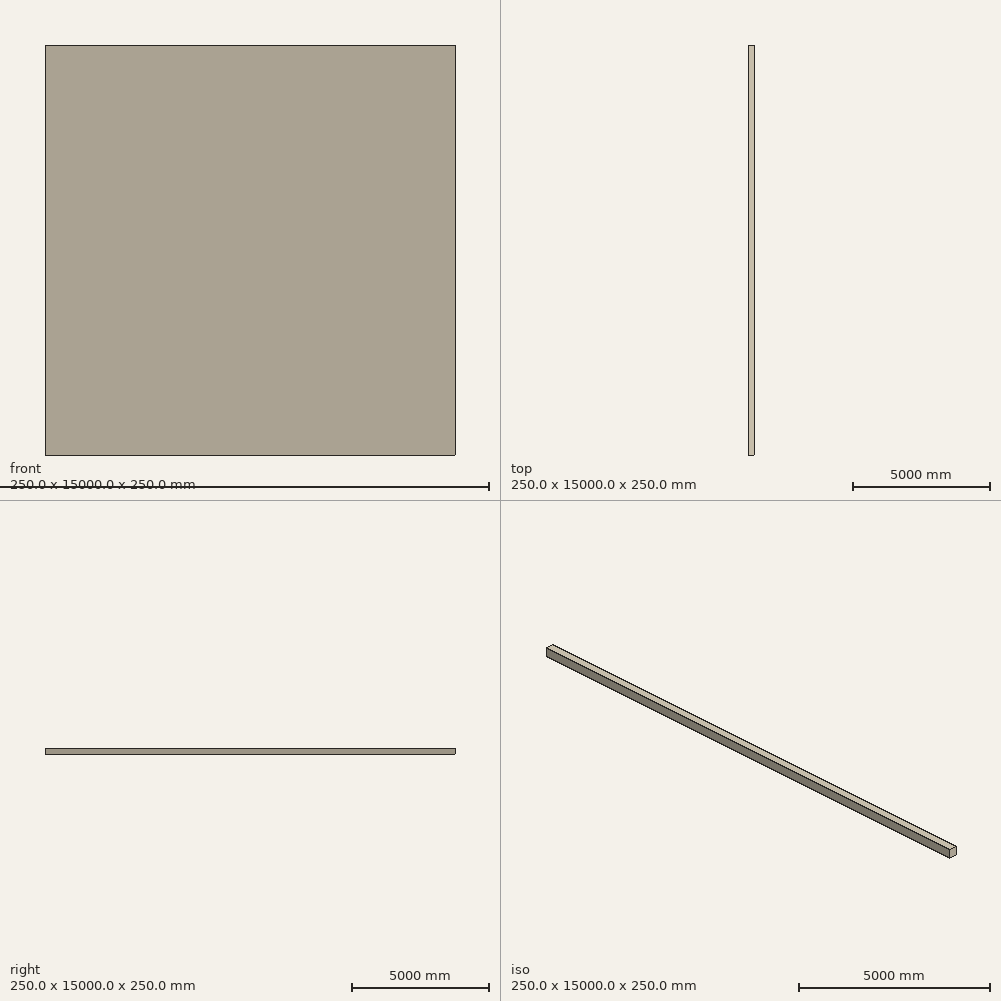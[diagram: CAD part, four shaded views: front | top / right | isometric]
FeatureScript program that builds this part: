
annotation { "Feature Type Name" : "Feature", "Feature Type Description" : "" }
export const myFeature = defineFeature(function(context is Context, id is Id, definition is map)
    precondition{}
    {
        {
            var Q0;
            Q0=qCreatedBy(makeId("Front.planeOp"),FACE);
            var sketch = newSketch(context, id + "F0", { "sketchPlane" : qUnion([Q0])});
            skLineSegment(sketch, "E0.bottom", {"start": v(-124.54, 145.9) * mm, "end": v(125.46, 145.9) * mm});
            skLineSegment(sketch, "E0.top", {"start": v(-124.54, -104.1) * mm, "end": v(125.46, -104.1) * mm});
            skLineSegment(sketch, "E0.left", {"start": v(-124.54, 145.9) * mm, "end": v(-124.54, -104.1) * mm});
            skLineSegment(sketch, "E0.right", {"start": v(125.46, 145.9) * mm, "end": v(125.46, -104.1) * mm});
            skSolve(sketch);
        }
        {
            var Q0;
            Q0=makeQuery(id+"F0.imprint","IMPRINT",FACE,{"disambiguationData":[TD([[makeQuery(id+"F0.imprint","IMPRINT",EDGE,{"derivedFrom":sQuery(id+"F0.wireOp",EDGE,"E0.bottom")}),-1.0]])]});
            extrude(context, id + "F1", {"entities" : qUnion([Q0]), "depth" : 15000 * mm});
        }
    });
